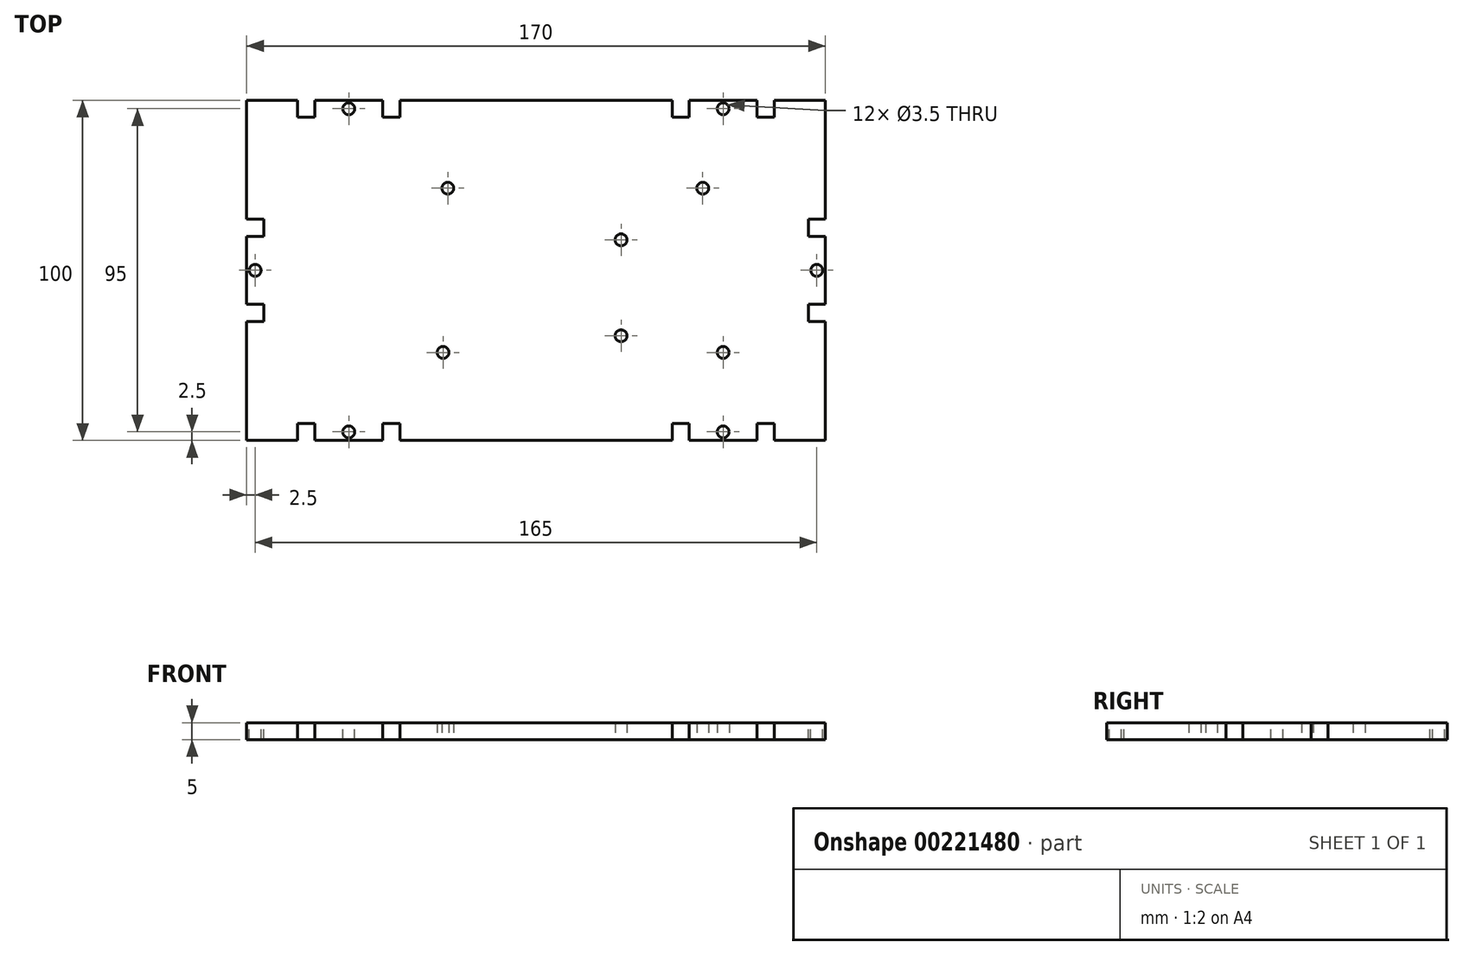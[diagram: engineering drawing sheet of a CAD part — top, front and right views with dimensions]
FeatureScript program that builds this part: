
annotation { "Feature Type Name" : "Feature", "Feature Type Description" : "" }
export const myFeature = defineFeature(function(context is Context, id is Id, definition is map)
    precondition{}
    {
        {
            assignVariable(context, id + "F0", {"name" : "thickness", "anyValue" : 5 * mm});
        }
        {
            var Q0;
            Q0=qCreatedBy(makeId("Top.planeOp"),FACE);
            var sketch = newSketch(context, id + "F1", { "sketchPlane" : qUnion([Q0])});
            skLineSegment(sketch, "E0.bottom", {"start": v(0, 0) * mm, "end": v(101.5, 0) * mm, "construction": true});
            skLineSegment(sketch, "E0.top", {"start": v(0, 53.5) * mm, "end": v(101.5, 53.5) * mm, "construction": true});
            skLineSegment(sketch, "E0.left", {"start": v(0, 0) * mm, "end": v(0, 53.5) * mm, "construction": true});
            skLineSegment(sketch, "E0.right", {"start": v(101.5, 0) * mm, "end": v(101.5, 53.5) * mm, "construction": true});
            skCircle(sketch, "E1", {"center": v(14.2, 2.6) * mm, "radius": 1.75 * mm});
            skCircle(sketch, "E2", {"center": v(15.6, 50.9) * mm, "radius": 1.75 * mm});
            skCircle(sketch, "E3", {"center": v(66.5, 35.7) * mm, "radius": 1.75 * mm});
            skCircle(sketch, "E4", {"center": v(66.5, 7.5) * mm, "radius": 1.75 * mm});
            skCircle(sketch, "E5", {"center": v(90.5, 50.9) * mm, "radius": 1.75 * mm});
            skCircle(sketch, "E6", {"center": v(96.5, 2.6) * mm, "radius": 1.75 * mm});
            skLineSegment(sketch, "E7.bottom", {"start": v(-43.5, 76.75) * mm, "end": v(126.5, 76.75) * mm});
            skLineSegment(sketch, "E7.top", {"start": v(-43.5, -23.25) * mm, "end": v(126.5, -23.25) * mm});
            skLineSegment(sketch, "E7.left", {"start": v(-43.5, 76.75) * mm, "end": v(-43.5, -23.25) * mm});
            skLineSegment(sketch, "E7.right", {"start": v(126.5, 76.75) * mm, "end": v(126.5, -23.25) * mm});
            skPoint(sketch, "E8", {"position": v(-43.5, 26.75) * mm});
            skPoint(sketch, "E9", {"position": v(0, 26.75) * mm});
            skPoint(sketch, "E10", {"position": v(41.5, 76.75) * mm});
            skSolve(sketch);
        }
        {
            var Q0;
            Q0 = qSketchRegion(id + "F1", true);
            extrude(context, id + "F2", {"entities" : qUnion([Q0]), "depth" : getVariable(context, 'thickness')});
        }
        {
            var Q0;
            Q0=makeQuery(id+"F2.opExtrude","CAP_FACE",FACE,{"disambiguationData":[OSD([sQuery(id+"F1.wireOp",EDGE,"E1"),sQuery(id+"F1.wireOp",EDGE,"E2"),sQuery(id+"F1.wireOp",EDGE,"E3"),sQuery(id+"F1.wireOp",EDGE,"E4"),sQuery(id+"F1.wireOp",EDGE,"E5"),sQuery(id+"F1.wireOp",EDGE,"E6"),sQuery(id+"F1.wireOp",EDGE,"E7.bottom"),sQuery(id+"F1.wireOp",EDGE,"E7.top"),sQuery(id+"F1.wireOp",EDGE,"E7.left"),sQuery(id+"F1.wireOp",EDGE,"E7.right")])],"isStart":false});
            var sketch = newSketch(context, id + "F3", { "sketchPlane" : qUnion([Q0])});
            skLineSegment(sketch, "E11.0", {"start": v(-38.5, 71.75) * mm, "end": v(-38.5, -18.25) * mm, "construction": true});
            skLineSegment(sketch, "E11.1", {"start": v(-38.5, 71.75) * mm, "end": v(121.5, 71.75) * mm, "construction": true});
            skLineSegment(sketch, "E11.2", {"start": v(121.5, 71.75) * mm, "end": v(121.5, -18.25) * mm, "construction": true});
            skLineSegment(sketch, "E11.3", {"start": v(-38.5, -18.25) * mm, "end": v(121.5, -18.25) * mm, "construction": true});
            skLineSegment(sketch, "E12.bottom", {"start": v(-28.5, -18.25) * mm, "end": v(-23.5, -18.25) * mm});
            skLineSegment(sketch, "E12.top", {"start": v(-28.5, -23.25) * mm, "end": v(-23.5, -23.25) * mm});
            skLineSegment(sketch, "E12.left", {"start": v(-28.5, -18.25) * mm, "end": v(-28.5, -23.25) * mm});
            skLineSegment(sketch, "E12.right", {"start": v(-23.5, -18.25) * mm, "end": v(-23.5, -23.25) * mm});
            skLineSegment(sketch, "E13.bottom", {"start": v(-3.5, -18.25) * mm, "end": v(1.5, -18.25) * mm});
            skLineSegment(sketch, "E13.top", {"start": v(-3.5, -23.25) * mm, "end": v(1.5, -23.25) * mm});
            skLineSegment(sketch, "E13.left", {"start": v(-3.5, -18.25) * mm, "end": v(-3.5, -23.25) * mm});
            skLineSegment(sketch, "E13.right", {"start": v(1.5, -18.25) * mm, "end": v(1.5, -23.25) * mm});
            skCircle(sketch, "E14", {"center": v(-13.5, -20.75) * mm, "radius": 1.75 * mm});
            skLineSegment(sketch, "E15", {"start": v(41.5, -23.25) * mm, "end": v(41.5, 76.75) * mm, "construction": true});
            skLineSegment(sketch, "E16.MirrorCS", {"start": v(81.5, -18.25) * mm, "end": v(81.5, -23.25) * mm});
            skCircle(sketch, "E17.MirrorC", {"center": v(96.5, -20.75) * mm, "radius": 1.75 * mm});
            skLineSegment(sketch, "E18.MirrorCS", {"start": v(86.5, -18.25) * mm, "end": v(86.5, -23.25) * mm});
            skLineSegment(sketch, "E19.MirrorCS", {"start": v(86.5, -23.25) * mm, "end": v(81.5, -23.25) * mm});
            skLineSegment(sketch, "E20.MirrorCS", {"start": v(86.5, -18.25) * mm, "end": v(81.5, -18.25) * mm});
            skLineSegment(sketch, "E21.MirrorCS", {"start": v(106.5, -18.25) * mm, "end": v(106.5, -23.25) * mm});
            skLineSegment(sketch, "E22.MirrorCS", {"start": v(111.5, -18.25) * mm, "end": v(111.5, -23.25) * mm});
            skLineSegment(sketch, "E23.MirrorCS", {"start": v(111.5, -23.25) * mm, "end": v(106.5, -23.25) * mm});
            skLineSegment(sketch, "E24.MirrorCS", {"start": v(111.5, -18.25) * mm, "end": v(106.5, -18.25) * mm});
            skLineSegment(sketch, "E25", {"start": v(-43.5, 26.75) * mm, "end": v(126.5, 26.75) * mm, "construction": true});
            skLineSegment(sketch, "E26.MirrorCS", {"start": v(111.5, 71.75) * mm, "end": v(106.5, 71.75) * mm});
            skLineSegment(sketch, "E27.MirrorCS", {"start": v(86.5, 76.75) * mm, "end": v(81.5, 76.75) * mm});
            skLineSegment(sketch, "E28.MirrorCS", {"start": v(106.5, 71.75) * mm, "end": v(106.5, 76.75) * mm});
            skLineSegment(sketch, "E29.MirrorCS", {"start": v(111.5, 76.75) * mm, "end": v(106.5, 76.75) * mm});
            skLineSegment(sketch, "E30.MirrorCS", {"start": v(111.5, 71.75) * mm, "end": v(111.5, 76.75) * mm});
            skLineSegment(sketch, "E31.MirrorCS", {"start": v(86.5, 71.75) * mm, "end": v(86.5, 76.75) * mm});
            skLineSegment(sketch, "E32.MirrorCS", {"start": v(-28.5, 76.75) * mm, "end": v(-23.5, 76.75) * mm});
            skLineSegment(sketch, "E33.MirrorCS", {"start": v(86.5, 71.75) * mm, "end": v(81.5, 71.75) * mm});
            skCircle(sketch, "E34.MirrorC", {"center": v(-13.5, 74.25) * mm, "radius": 1.75 * mm});
            skLineSegment(sketch, "E35.MirrorCS", {"start": v(-28.5, 71.75) * mm, "end": v(-23.5, 71.75) * mm});
            skLineSegment(sketch, "E36.MirrorCS", {"start": v(1.5, 71.75) * mm, "end": v(1.5, 76.75) * mm});
            skCircle(sketch, "E37.MirrorC", {"center": v(96.5, 74.25) * mm, "radius": 1.75 * mm});
            skLineSegment(sketch, "E38.MirrorCS", {"start": v(-3.5, 71.75) * mm, "end": v(-3.5, 76.75) * mm});
            skLineSegment(sketch, "E39.MirrorCS", {"start": v(-3.5, 76.75) * mm, "end": v(1.5, 76.75) * mm});
            skLineSegment(sketch, "E40.MirrorCS", {"start": v(-23.5, 71.75) * mm, "end": v(-23.5, 76.75) * mm});
            skLineSegment(sketch, "E41.MirrorCS", {"start": v(-28.5, 71.75) * mm, "end": v(-28.5, 76.75) * mm});
            skLineSegment(sketch, "E42.MirrorCS", {"start": v(-3.5, 71.75) * mm, "end": v(1.5, 71.75) * mm});
            skLineSegment(sketch, "E43.MirrorCS", {"start": v(81.5, 71.75) * mm, "end": v(81.5, 76.75) * mm});
            skLineSegment(sketch, "E44.bottom", {"start": v(-38.5, 41.75) * mm, "end": v(-38.5, 36.75) * mm});
            skLineSegment(sketch, "E44.top", {"start": v(-43.5, 41.75) * mm, "end": v(-43.5, 36.75) * mm});
            skLineSegment(sketch, "E44.left", {"start": v(-38.5, 41.75) * mm, "end": v(-43.5, 41.75) * mm});
            skLineSegment(sketch, "E44.right", {"start": v(-38.5, 36.75) * mm, "end": v(-43.5, 36.75) * mm});
            skLineSegment(sketch, "E45.bottom", {"start": v(-38.5, 16.75) * mm, "end": v(-38.5, 11.75) * mm});
            skLineSegment(sketch, "E45.top", {"start": v(-43.5, 16.75) * mm, "end": v(-43.5, 11.75) * mm});
            skLineSegment(sketch, "E45.left", {"start": v(-38.5, 16.75) * mm, "end": v(-43.5, 16.75) * mm});
            skLineSegment(sketch, "E45.right", {"start": v(-38.5, 11.75) * mm, "end": v(-43.5, 11.75) * mm});
            skCircle(sketch, "E46", {"center": v(-41, 26.75) * mm, "radius": 1.75 * mm});
            skLineSegment(sketch, "E47.MirrorCS", {"start": v(121.5, 36.75) * mm, "end": v(126.5, 36.75) * mm});
            skLineSegment(sketch, "E48.MirrorCS", {"start": v(121.5, 11.75) * mm, "end": v(126.5, 11.75) * mm});
            skLineSegment(sketch, "E49.MirrorCS", {"start": v(121.5, 41.75) * mm, "end": v(126.5, 41.75) * mm});
            skLineSegment(sketch, "E50.MirrorCS", {"start": v(126.5, 16.75) * mm, "end": v(126.5, 11.75) * mm});
            skLineSegment(sketch, "E51.MirrorCS", {"start": v(126.5, 41.75) * mm, "end": v(126.5, 36.75) * mm});
            skLineSegment(sketch, "E52.MirrorCS", {"start": v(121.5, 16.75) * mm, "end": v(126.5, 16.75) * mm});
            skLineSegment(sketch, "E53.MirrorCS", {"start": v(121.5, 41.75) * mm, "end": v(121.5, 36.75) * mm});
            skCircle(sketch, "E54.MirrorC", {"center": v(124, 26.75) * mm, "radius": 1.75 * mm});
            skLineSegment(sketch, "E55.MirrorCS", {"start": v(121.5, 16.75) * mm, "end": v(121.5, 11.75) * mm});
            skSolve(sketch);
        }
        {
            var Q0;
            Q0 = qSketchRegion(id + "F3", true);
            var Q1;
            Q1=makeQuery(id+"F2.opExtrude","CAP_FACE",FACE,{"disambiguationData":[OSD([sQuery(id+"F1.wireOp",EDGE,"E1"),sQuery(id+"F1.wireOp",EDGE,"E2"),sQuery(id+"F1.wireOp",EDGE,"E3"),sQuery(id+"F1.wireOp",EDGE,"E4"),sQuery(id+"F1.wireOp",EDGE,"E5"),sQuery(id+"F1.wireOp",EDGE,"E6"),sQuery(id+"F1.wireOp",EDGE,"E7.bottom"),sQuery(id+"F1.wireOp",EDGE,"E7.top"),sQuery(id+"F1.wireOp",EDGE,"E7.left"),sQuery(id+"F1.wireOp",EDGE,"E7.right")])],"isStart":true});
            extrude(context, id + "F4", {"entities" : qUnion([Q0]), "operationType" : NewBodyOperationType.REMOVE, "endBound" : BoundingType.UP_TO_SURFACE, "oppositeDirection" : true, "endBoundEntityFace" : qUnion([Q1]), "depth" : 25 * mm});
        }
    });
